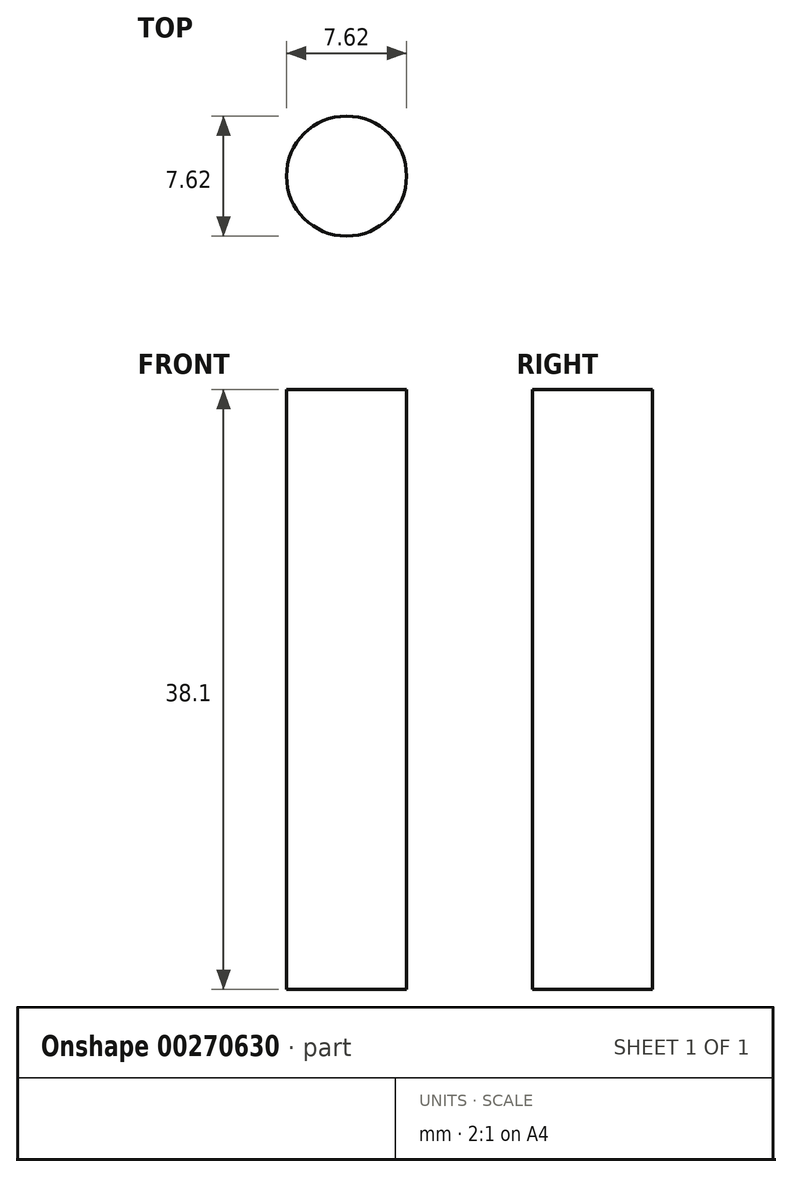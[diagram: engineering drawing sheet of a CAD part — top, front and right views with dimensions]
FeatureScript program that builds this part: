
annotation { "Feature Type Name" : "Feature", "Feature Type Description" : "" }
export const myFeature = defineFeature(function(context is Context, id is Id, definition is map)
    precondition{}
    {
        {
            var Q0;
            Q0=qCreatedBy(makeId("Top.planeOp"),FACE);
            var sketch = newSketch(context, id + "F0", { "sketchPlane" : qUnion([Q0])});
            skCircle(sketch, "E0", {"center": v(0, 0) * mm, "radius": 3.81 * mm});
            skSolve(sketch);
        }
        {
            var Q0;
            Q0 = qSketchRegion(id + "F0", true);
            extrude(context, id + "F1", {"entities" : qUnion([Q0]), "depth" : 38.1 * mm});
        }
    });
